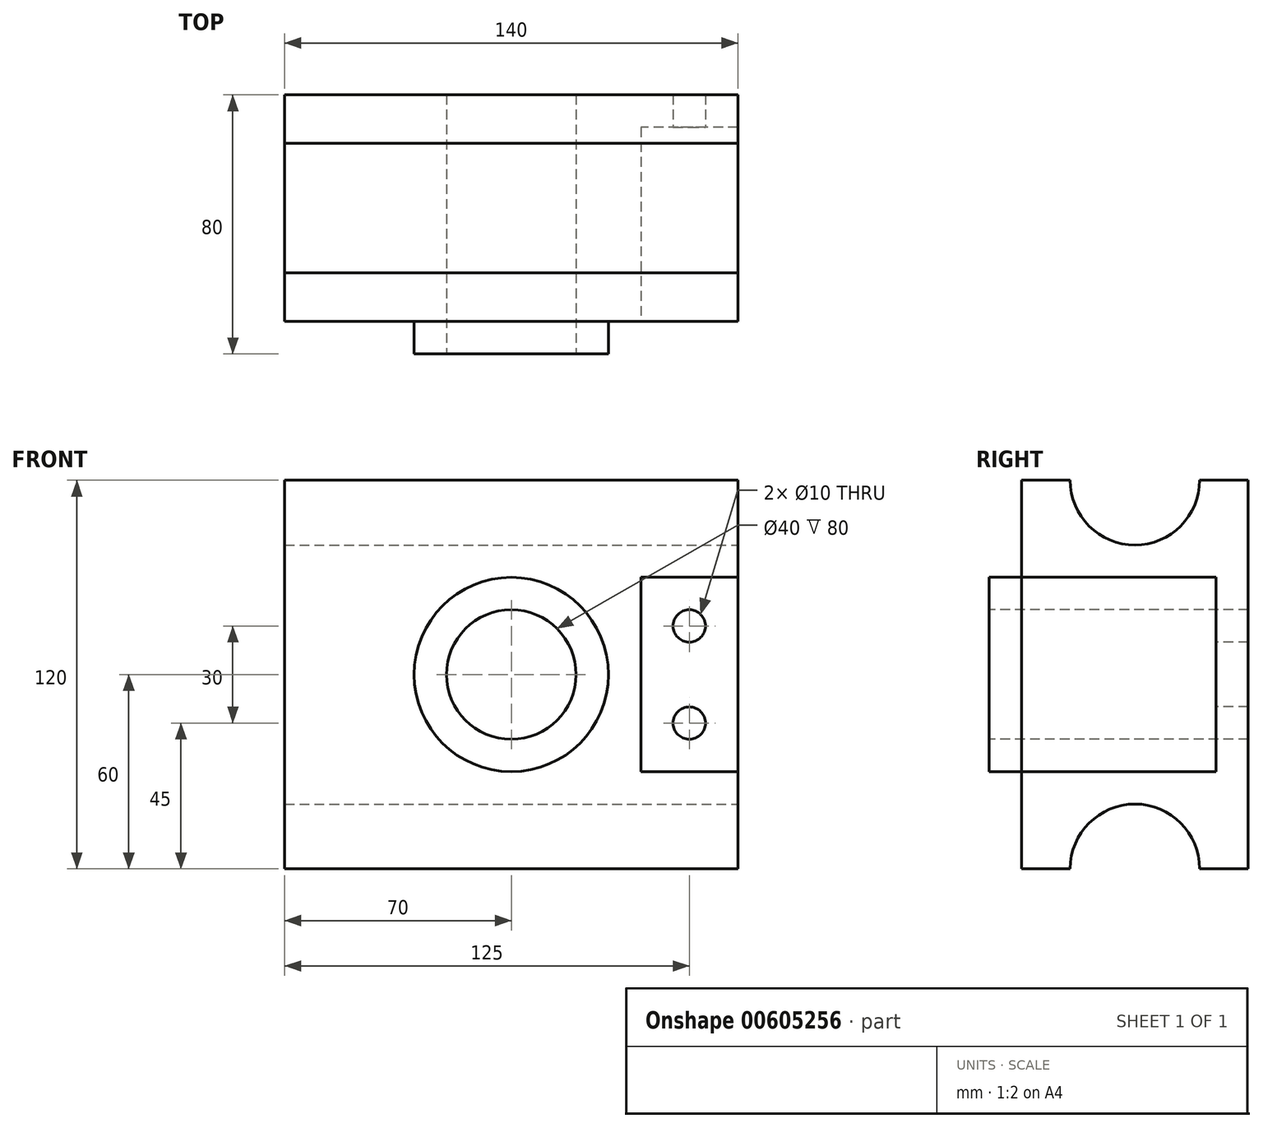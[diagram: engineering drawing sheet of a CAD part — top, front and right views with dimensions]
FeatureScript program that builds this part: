
annotation { "Feature Type Name" : "Feature", "Feature Type Description" : "" }
export const myFeature = defineFeature(function(context is Context, id is Id, definition is map)
    precondition{}
    {
        {
            var Q0;
            Q0=qCreatedBy(makeId("Front.planeOp"),FACE);
            var sketch = newSketch(context, id + "F0", { "sketchPlane" : qUnion([Q0])});
            skLineSegment(sketch, "E0.bottom", {"start": v(70, -30) * mm, "end": v(-70, -30) * mm});
            skLineSegment(sketch, "E0.top", {"start": v(70, 30) * mm, "end": v(-70, 30) * mm});
            skLineSegment(sketch, "E0.left", {"start": v(70, -30) * mm, "end": v(70, 30) * mm});
            skLineSegment(sketch, "E0.right", {"start": v(-70, -30) * mm, "end": v(-70, 30) * mm});
            skPoint(sketch, "E0.middle", {"position": v(0, 0) * mm});
            skSolve(sketch);
        }
        {
            var Q0;
            Q0 = qSketchRegion(id + "F0", true);
            extrude(context, id + "F1", {"entities" : qUnion([Q0]), "endBound" : BoundingType.SYMMETRIC, "depth" : 70 * mm, "offsetDistance" : 25 * mm});
        }
        {
            var Q0;
            Q0=makeQuery(id+"F1.opExtrude","SWEPT_FACE",FACE,{"disambiguationData":[OSD([sQuery(id+"F0.wireOp",EDGE,"E0.left")])]});
            var sketch = newSketch(context, id + "F2", { "sketchPlane" : qUnion([Q0])});
            skCircle(sketch, "E1", {"center": v(0, -30) * mm, "radius": 20 * mm});
            skSolve(sketch);
        }
        {
            var Q0;
            {var subQ0=sQuery(id+"F2.wireOp",EDGE,"E1");var subQ1=makeQuery(id+"F1.opExtrude","SWEPT_EDGE",EDGE,{"disambiguationData":[OSD([sQuery(id+"F0.wireOp",EDGE,"E0.bottom"),sQuery(id+"F0.wireOp",EDGE,"E0.left")])]});var subQ2=makeQuery(id+"F2.imprint","INTERSECT",VERTEX,{"disambiguationData":[OD(0.0)],"derivedFrom":[subQ1,subQ0]});Q0=makeQuery(id+"F2.imprint","IMPRINT",FACE,{"disambiguationData":[TD([[makeQuery(id+"F2.imprint","IMPRINT",EDGE,{"disambiguationData":[TD([[subQ2,1.0]])],"derivedFrom":subQ0}),1.0]])]});}
            var Q1;
            {var subQ0=sQuery(id+"F2.wireOp",EDGE,"E1");var subQ1=makeQuery(id+"F1.opExtrude","SWEPT_EDGE",EDGE,{"disambiguationData":[OSD([sQuery(id+"F0.wireOp",EDGE,"E0.bottom"),sQuery(id+"F0.wireOp",EDGE,"E0.left")])]});var subQ2=makeQuery(id+"F2.imprint","INTERSECT",VERTEX,{"disambiguationData":[OD(0.0)],"derivedFrom":[subQ1,subQ0]});Q1=makeQuery(id+"F2.imprint","IMPRINT",FACE,{"disambiguationData":[TD([[makeQuery(id+"F2.imprint","IMPRINT",EDGE,{"disambiguationData":[TD([[subQ2,-1.0]])],"derivedFrom":subQ0}),1.0]])]});}
            extrude(context, id + "F3", {"entities" : qUnion([Q0, Q1]), "operationType" : NewBodyOperationType.REMOVE, "endBound" : BoundingType.THROUGH_ALL, "oppositeDirection" : true, "depth" : 25 * mm, "offsetDistance" : 25 * mm});
        }
        {
            var Q0;
            Q0=makeQuery(id+"F1.opExtrude","CAP_FACE",FACE,{"disambiguationData":[OSD([sQuery(id+"F0.wireOp",EDGE,"E0.bottom"),sQuery(id+"F0.wireOp",EDGE,"E0.top"),sQuery(id+"F0.wireOp",EDGE,"E0.left"),sQuery(id+"F0.wireOp",EDGE,"E0.right")])],"isStart":false});
            var sketch = newSketch(context, id + "F4", { "sketchPlane" : qUnion([Q0])});
            skLineSegment(sketch, "E2.bottom", {"start": v(70, 30) * mm, "end": v(40, 30) * mm});
            skLineSegment(sketch, "E2.top", {"start": v(70, 0) * mm, "end": v(40, 0) * mm});
            skLineSegment(sketch, "E2.left", {"start": v(70, 30) * mm, "end": v(70, 0) * mm});
            skLineSegment(sketch, "E2.right", {"start": v(40, 30) * mm, "end": v(40, 0) * mm});
            skSolve(sketch);
        }
        {
            var Q0;
            Q0=makeQuery(id+"F4.imprint","IMPRINT",FACE,{"disambiguationData":[TD([[makeQuery(id+"F4.imprint","IMPRINT",EDGE,{"derivedFrom":sQuery(id+"F4.wireOp",EDGE,"E2.bottom")}),1.0]])]});
            extrude(context, id + "F5", {"entities" : qUnion([Q0]), "operationType" : NewBodyOperationType.REMOVE, "oppositeDirection" : true, "depth" : 60 * mm, "offsetDistance" : 25 * mm});
        }
        {
            var Q0;
            Q0=makeQuery(id+"F1.opExtrude","CAP_FACE",FACE,{"disambiguationData":[OSD([sQuery(id+"F0.wireOp",EDGE,"E0.bottom"),sQuery(id+"F0.wireOp",EDGE,"E0.top"),sQuery(id+"F0.wireOp",EDGE,"E0.left"),sQuery(id+"F0.wireOp",EDGE,"E0.right")])],"isStart":false});
            var sketch = newSketch(context, id + "F6", { "sketchPlane" : qUnion([Q0])});
            skCircle(sketch, "E3", {"center": v(0, 30) * mm, "radius": 20 * mm});
            skSolve(sketch);
        }
        {
            var Q0;
            Q0 = qSketchRegion(id + "F6", true);
            extrude(context, id + "F7", {"entities" : qUnion([Q0]), "operationType" : NewBodyOperationType.REMOVE, "oppositeDirection" : true, "depth" : 72.1 * mm, "offsetDistance" : 25 * mm});
        }
        {
            var Q0;
            Q0=makeQuery(id+"F1.opExtrude","CAP_FACE",FACE,{"disambiguationData":[OSD([sQuery(id+"F0.wireOp",EDGE,"E0.bottom"),sQuery(id+"F0.wireOp",EDGE,"E0.top"),sQuery(id+"F0.wireOp",EDGE,"E0.left"),sQuery(id+"F0.wireOp",EDGE,"E0.right")])],"isStart":false});
            var sketch = newSketch(context, id + "F8", { "sketchPlane" : qUnion([Q0])});
            skArc(sketch, "E4", {"start": v(-30, 30) * mm, "mid": v(0, 0) * mm, "end": v(30, 30) * mm});
            skLineSegment(sketch, "E5", {"start": v(0, 30) * mm, "end": v(36.4, 30) * mm});
            skLineSegment(sketch, "E6", {"start": v(0, 30) * mm, "end": v(-57.94, 30) * mm});
            skSolve(sketch);
        }
        {
            var Q0;
            Q0 = qSketchRegion(id + "F8", true);
            extrude(context, id + "F9", {"entities" : qUnion([Q0]), "operationType" : NewBodyOperationType.ADD, "depth" : 10 * mm, "offsetDistance" : 25 * mm});
        }
        {
            var Q0;
            Q0=makeQuery(id+"F9.opExtrude","CAP_FACE",FACE,{"disambiguationData":[OSD([sQuery(id+"F8.wireOp",EDGE,"E4"),sQuery(id+"F8.wireOp",EDGE,"E5"),sQuery(id+"F8.wireOp",EDGE,"E6")])],"isStart":true});
            var sketch = newSketch(context, id + "F10", { "sketchPlane" : qUnion([Q0])});
            skCircle(sketch, "E7", {"center": v(0, 30) * mm, "radius": 20 * mm});
            skSolve(sketch);
        }
        {
            var Q0;
            Q0=makeQuery(id+"F10.imprint","IMPRINT",FACE,{"disambiguationData":[TD([[makeQuery(id+"F10.imprint","IMPRINT",EDGE,{"disambiguationData":[OD(0.0)],"derivedFrom":sQuery(id+"F10.wireOp",EDGE,"E7")}),1.0]])]});
            var Q1;
            Q1=makeQuery(id+"F10.imprint","IMPRINT",FACE,{"disambiguationData":[TD([[makeQuery(id+"F10.imprint","IMPRINT",EDGE,{"disambiguationData":[OD(1.0)],"derivedFrom":sQuery(id+"F10.wireOp",EDGE,"E7")}),-1.0]])]});
            extrude(context, id + "F11", {"entities" : qUnion([Q0, Q1]), "operationType" : NewBodyOperationType.REMOVE, "oppositeDirection" : true, "depth" : 25 * mm, "offsetDistance" : 25 * mm});
        }
        {
            var Q0;
            Q0=makeQuery(id+"F5.boolean.opBoolean","COPY",FACE,{"derivedFrom":makeQuery(id+"F5.opExtrude","CAP_FACE",FACE,{"disambiguationData":[OSD([sQuery(id+"F4.wireOp",EDGE,"E2.bottom"),sQuery(id+"F4.wireOp",EDGE,"E2.top"),sQuery(id+"F4.wireOp",EDGE,"E2.left"),sQuery(id+"F4.wireOp",EDGE,"E2.right")])],"isStart":false})});
            var sketch = newSketch(context, id + "F12", { "sketchPlane" : qUnion([Q0])});
            skCircle(sketch, "E8", {"center": v(55, 15) * mm, "radius": 5 * mm});
            skSolve(sketch);
        }
        {
            var Q0;
            Q0 = qSketchRegion(id + "F12", true);
            extrude(context, id + "F13", {"entities" : qUnion([Q0]), "operationType" : NewBodyOperationType.REMOVE, "oppositeDirection" : true, "depth" : 25 * mm, "offsetDistance" : 25 * mm});
        }
        {
            var Q0;
            Q0=qCreatedBy(makeId("Top.planeOp"),FACE);
            cPlane(context, id + "F14", {"entities" : qUnion([Q0]), "cplaneType" : CPlaneType.OFFSET, "offset" : 30 * mm, "width" : 150 * mm, "height" : 150 * mm});
        }
        {
            var Q0;
            Q0=makeQuery(id+"F1.opExtrude","SWEPT_BODY",BODY,{"disambiguationData":[OSD([sQuery(id+"F0.wireOp",EDGE,"E0.bottom"),sQuery(id+"F0.wireOp",EDGE,"E0.top"),sQuery(id+"F0.wireOp",EDGE,"E0.left"),sQuery(id+"F0.wireOp",EDGE,"E0.right")])]});
            var Q1;
            Q1=qCreatedBy(id+"F14.planeOp",FACE);
            mirror(context, id + "F15", {"operationType" : NewBodyOperationType.ADD, "entities" : qUnion([Q0]), "mirrorPlane" : qUnion([Q1])});
        }
    });
